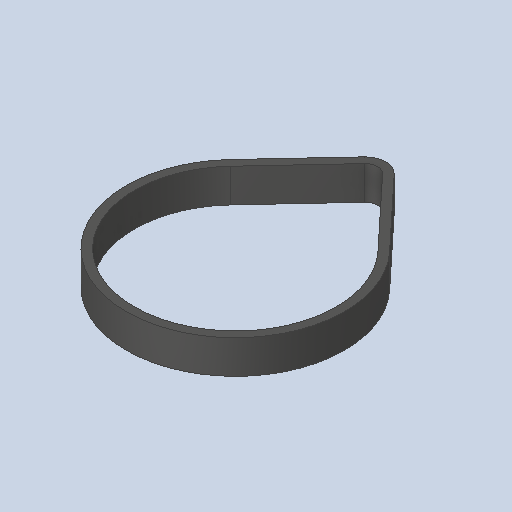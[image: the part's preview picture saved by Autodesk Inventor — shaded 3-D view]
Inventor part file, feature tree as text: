
AUTODESK INVENTOR PART (.ipt)
format: ipt  version: 2023.4 (Build 274418000, 418)  size: 95,744 bytes
history: native  units: in
note: dims shown in document units (in); Inventor stores cm internally (conversion verified against a paired STEP export)
features: extrude x1
ambient origin geometry x8: Origin, YZ Plane, XZ Plane, XY Plane, X Axis, Y Axis, Z Axis, Center Point
bodies: Solid1 (feature_tree)
feature tree (1):
  extrude  "Extrude-Thin1"  [1 undecoded]
note: 1 required parameter value undecoded (feature->parameter linkage not recoverable at this tier; creation-order binding heuristic only, values carry confidence <= 0.55)
